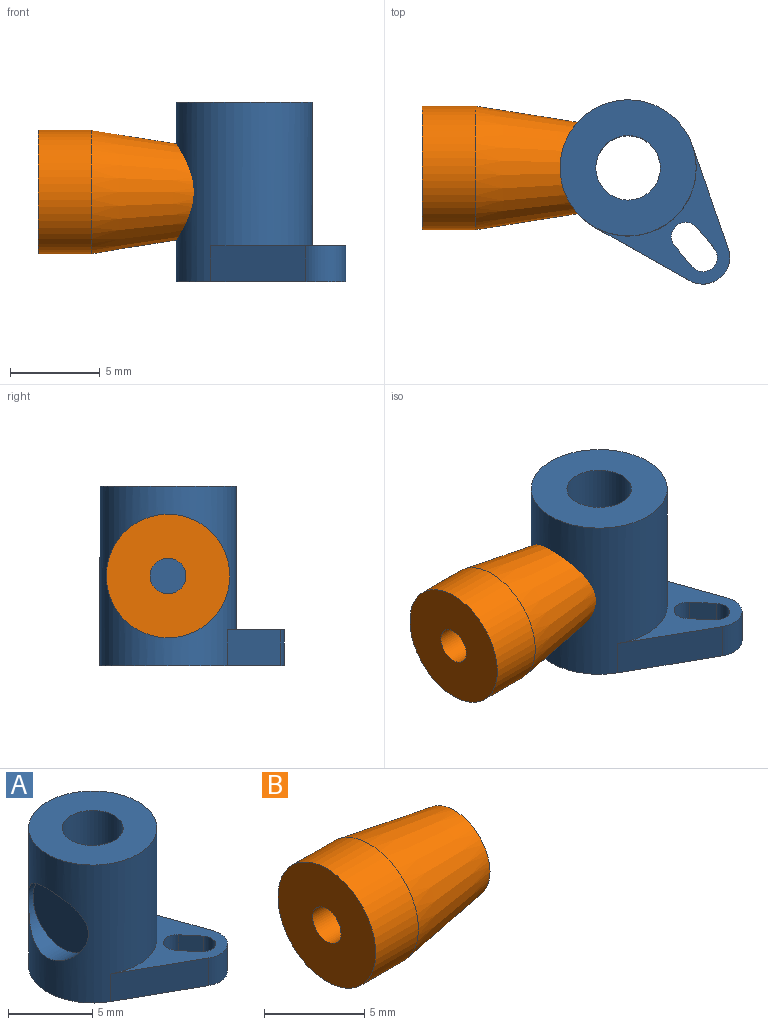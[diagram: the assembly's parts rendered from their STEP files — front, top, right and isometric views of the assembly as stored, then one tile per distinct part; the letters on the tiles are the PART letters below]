
ASSEMBLY  parts=2 mates=1
PART A: 14 faces, bbox 9.5x10.3x10 mm
  f0: cylinder r=3.8mm len=10mm, axis (0,0,-1), area 199.5mm2, adj f2,f3,f4,f7,f12,f13
  f1: cylinder r=1.8mm len=10mm, axis (0,0,-1), area 113.1mm2, adj f2,f3
  f2: plane 7.6x7.6mm, normal (0,0,1), area 35.2mm2, adj f0,f1
  f3: plane 10.28x9.48mm, normal (0,0,-1), area 48.3mm2, adj f0,f1,f6,f7,f8,f9,f10,f11
  f4: cylinder r=2.5mm len=5mm, axis (1,0,0), area 13.3mm2, adj f0,f5
  f5: plane 5x5mm, normal (-1,0,0), area 19.6mm2, adj f4
  f6: cylinder r=1.5mm len=2.23mm, axis (0,0,-1), area 7.3mm2, adj f3,f7,f12,f13
  f7: plane 5.3x2.97mm, normal (-0.49,-0.87,0), area 12.2mm2, adj f0,f3,f6,f13
  f8: plane 2x1.15mm, normal (-0.77,-0.64,0), area 3mm2, adj f3,f9,f11,f13
  f9: cylinder r=0.8mm len=2mm, axis (0,0,-1), area 5mm2, adj f3,f8,f10,f13
  f10: plane 2x1.15mm, normal (0.77,0.64,0), area 3mm2, adj f3,f9,f11,f13
  f11: cylinder r=0.8mm len=2mm, axis (0,0,-1), area 5mm2, adj f3,f8,f10,f13
  f12: plane 5.74x2.01mm, normal (0.94,0.33,0), area 12.2mm2, adj f0,f3,f6,f13
  f13: plane 7.73x7.54mm, normal (0,0,1), area 13.1mm2, adj f0,f6,f7,f8,f9,f10,f11,f12
PART B: 5 faces, bbox 9x6.9x6.9 mm
  f0: cone r=2.5mm half-angle=9deg, axis (-1,0,0), area 113.6mm2, adj f1,f3
  f1: plane 5x5mm, normal (1,0,0), area 16.5mm2, adj f0,f2
  f2: cylinder r=1mm len=9mm, axis (-1,0,0), area 56.5mm2, adj f1,f4
  f3: cylinder r=3.45mm len=6.9mm, axis (1,0,0), area 65mm2, adj f0,f4
  f4: plane 6.9x6.9mm, normal (-1,0,0), area 34.3mm2, adj f2,f3
PLACE A rot(axis=(0,0,-1),0deg) t=(0,0,0)mm
PLACE B rot(axis=(-0.01,0.01,-1),0deg) t=(0,0,0)mm
MATE fastened B.f0 <-> A.f4  axis (1,0,0) through (-11.5,156,-7.5)mm
